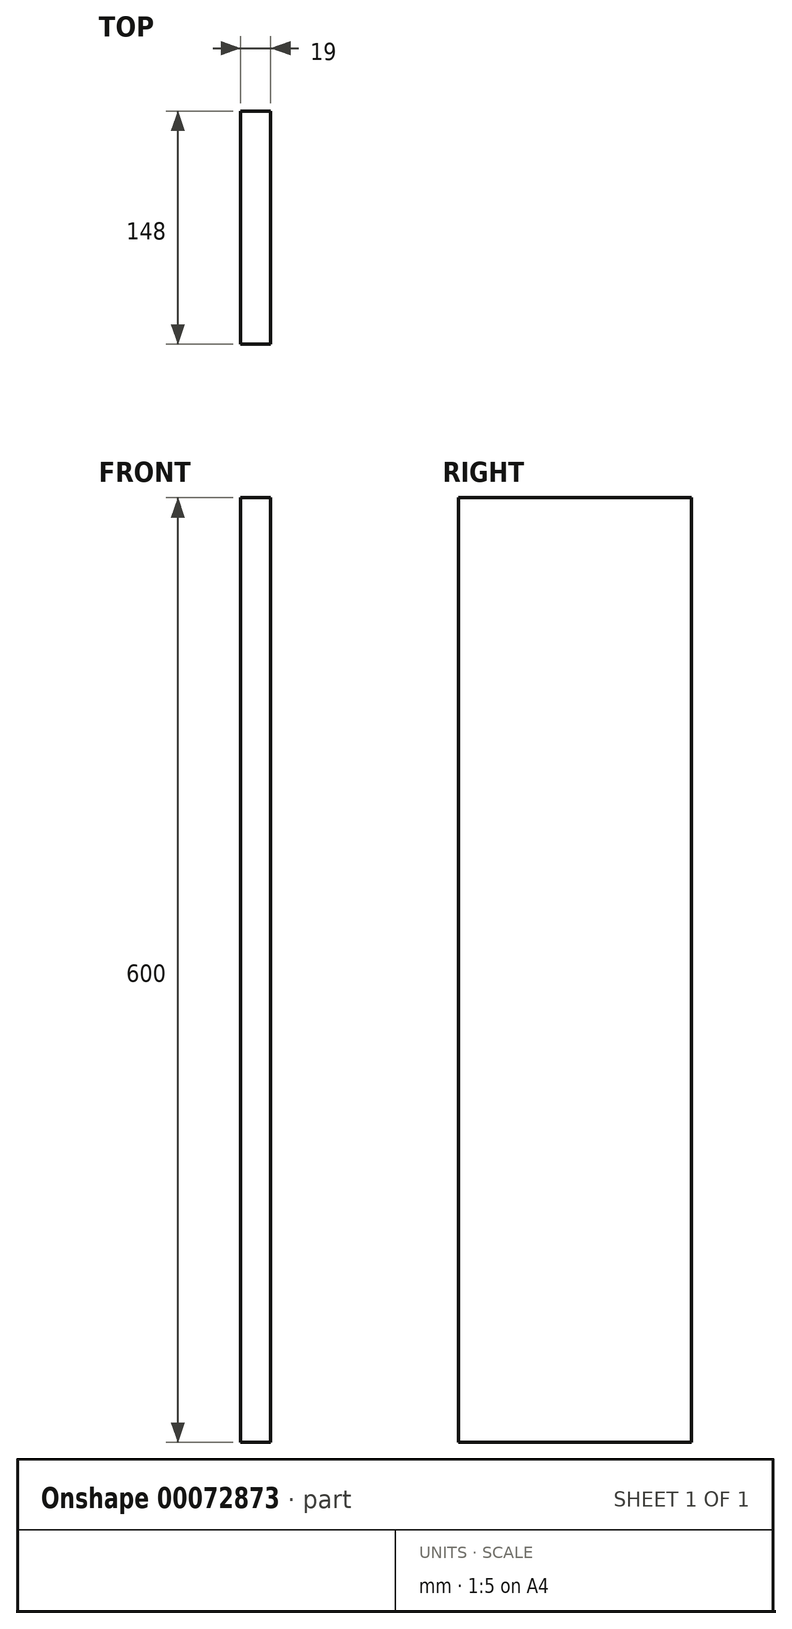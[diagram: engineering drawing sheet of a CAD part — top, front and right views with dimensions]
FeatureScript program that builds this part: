
annotation { "Feature Type Name" : "Feature", "Feature Type Description" : "" }
export const myFeature = defineFeature(function(context is Context, id is Id, definition is map)
    precondition{}
    {
        {
            var Q0;
            Q0=qCreatedBy(makeId("Right.planeOp"),FACE);
            var sketch = newSketch(context, id + "F0", { "sketchPlane" : qUnion([Q0])});
            skLineSegment(sketch, "E0.bottom", {"start": v(0, 0) * mm, "end": v(-148, 0) * mm});
            skLineSegment(sketch, "E0.top", {"start": v(0, -600) * mm, "end": v(-148, -600) * mm});
            skLineSegment(sketch, "E0.left", {"start": v(0, 0) * mm, "end": v(0, -600) * mm});
            skLineSegment(sketch, "E0.right", {"start": v(-148, 0) * mm, "end": v(-148, -600) * mm});
            skSolve(sketch);
        }
        {
            var Q0;
            Q0=makeQuery(id+"F0.imprint","IMPRINT",FACE,{"disambiguationData":[TD([[makeQuery(id+"F0.imprint","IMPRINT",EDGE,{"derivedFrom":sQuery(id+"F0.wireOp",EDGE,"E0.bottom")}),1.0]])]});
            extrude(context, id + "F1", {"entities" : qUnion([Q0]), "depth" : 19 * mm});
        }
    });
